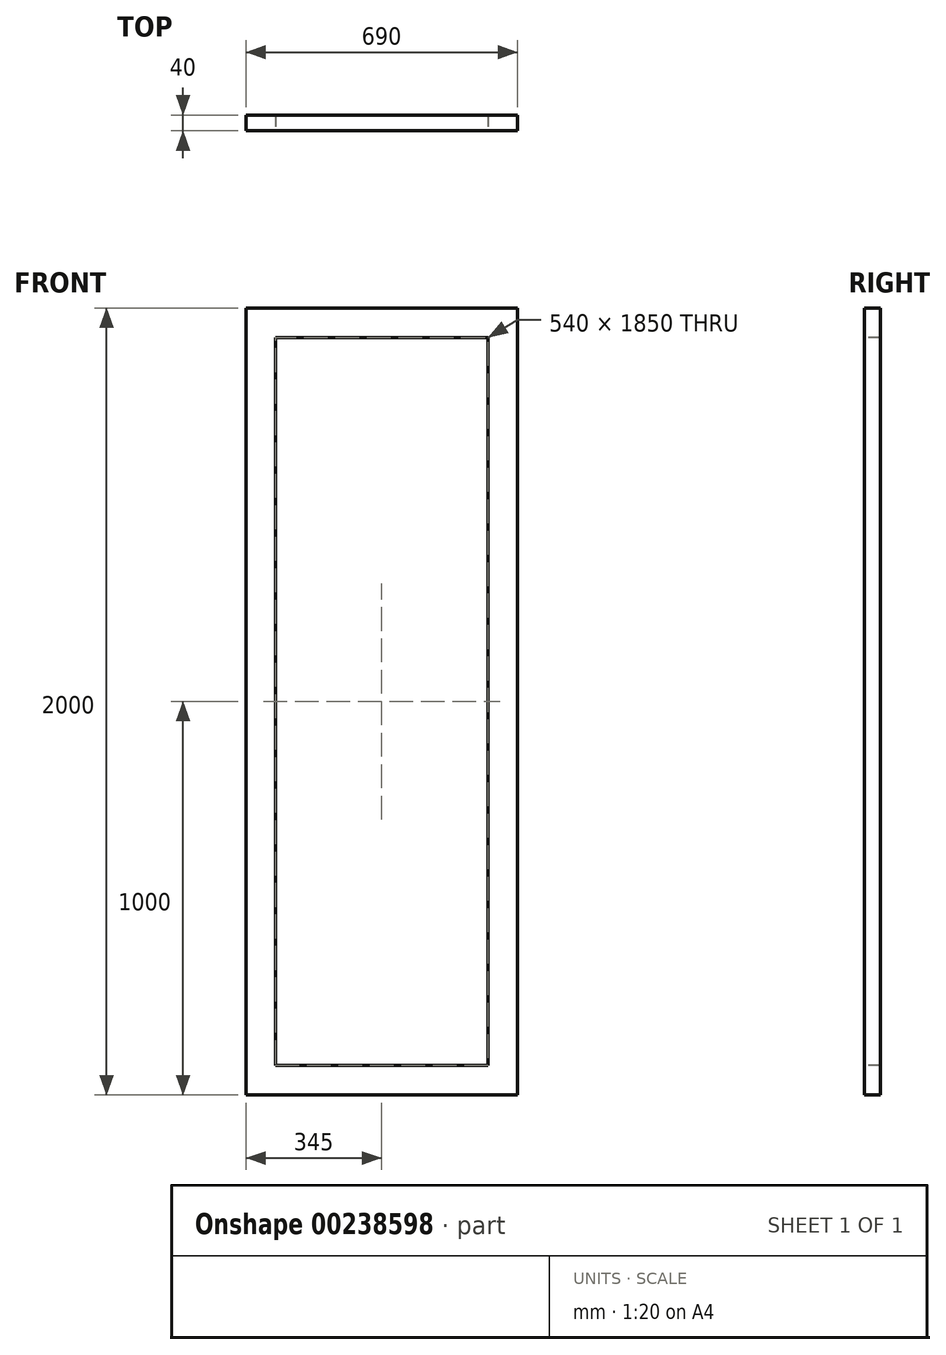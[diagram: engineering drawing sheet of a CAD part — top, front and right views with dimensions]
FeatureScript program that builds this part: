
annotation { "Feature Type Name" : "Feature", "Feature Type Description" : "" }
export const myFeature = defineFeature(function(context is Context, id is Id, definition is map)
    precondition{}
    {
        {
            var Q0;
            Q0=qCreatedBy(makeId("Front.planeOp"),FACE);
            var sketch = newSketch(context, id + "F0", { "sketchPlane" : qUnion([Q0])});
            skLineSegment(sketch, "E0.bottom", {"start": v(345, -1000) * mm, "end": v(-345, -1000) * mm});
            skLineSegment(sketch, "E0.top", {"start": v(345, 1000) * mm, "end": v(-345, 1000) * mm});
            skLineSegment(sketch, "E0.left", {"start": v(345, -1000) * mm, "end": v(345, 1000) * mm});
            skLineSegment(sketch, "E0.right", {"start": v(-345, -1000) * mm, "end": v(-345, 1000) * mm});
            skPoint(sketch, "E0.middle", {"position": v(0, 0) * mm});
            skSolve(sketch);
        }
        {
            var Q0;
            Q0=makeQuery(id+"F0.imprint","IMPRINT",FACE,{"disambiguationData":[TD([[makeQuery(id+"F0.imprint","IMPRINT",EDGE,{"derivedFrom":sQuery(id+"F0.wireOp",EDGE,"E0.bottom")}),-1.0]])]});
            extrude(context, id + "F1", {"entities" : qUnion([Q0]), "depth" : 40 * mm});
        }
        {
            var Q0;
            Q0=makeQuery(id+"F1.opExtrude","CAP_FACE",FACE,{"disambiguationData":[OSD([sQuery(id+"F0.wireOp",EDGE,"E0.bottom"),sQuery(id+"F0.wireOp",EDGE,"E0.top"),sQuery(id+"F0.wireOp",EDGE,"E0.left"),sQuery(id+"F0.wireOp",EDGE,"E0.right")])],"isStart":false});
            var sketch = newSketch(context, id + "F2", { "sketchPlane" : qUnion([Q0])});
            skLineSegment(sketch, "E1.bottom", {"start": v(-270, 925) * mm, "end": v(270, 925) * mm});
            skLineSegment(sketch, "E1.top", {"start": v(-270, -925) * mm, "end": v(270, -925) * mm});
            skLineSegment(sketch, "E1.left", {"start": v(-270, 925) * mm, "end": v(-270, -925) * mm});
            skLineSegment(sketch, "E1.right", {"start": v(270, 925) * mm, "end": v(270, -925) * mm});
            skPoint(sketch, "E1.middle", {"position": v(0, 0) * mm});
            skSolve(sketch);
        }
        {
            var Q0;
            Q0=qSketchRegion(id+"F2",true);
            var Q1;
            Q1=sQuery(id+"F2.wireOp",EDGE,"E1.bottom");
            extrude(context, id + "F3", {"entities" : qUnion([Q0]), "operationType" : NewBodyOperationType.REMOVE, "surfaceEntities" : qUnion([Q1]), "endBound" : BoundingType.THROUGH_ALL, "oppositeDirection" : true, "depth" : 25 * mm});
        }
    });
